annotation { "Feature Type Name" : "Feature", "Feature Type Description" : "" }
export const myFeature = defineFeature(function(context is Context, id is Id, definition is map)
    precondition{}
    {
        {
            var Q0;
            Q0=qCreatedBy(makeId("Front.planeOp"),FACE);
            var sketch = newSketch(context, id + "F0", { "sketchPlane" : qUnion([Q0])});
            skLineSegment(sketch, "E0.bottom", {"start": v(-78.74, 0) * mm, "end": v(0, 0) * mm});
            skLineSegment(sketch, "E0.top", {"start": v(-56.51, 177.8) * mm, "end": v(0, 177.8) * mm});
            skLineSegment(sketch, "E0.left", {"start": v(0, 177.8) * mm, "end": v(0, 0) * mm});
            skLineSegment(sketch, "E0.right", {"start": v(-78.74, 155.58) * mm, "end": v(-78.74, 0) * mm});
            skArc(sketch, "E1", {"start": v(-56.51, 177.8) * mm, "mid": v(-72.23, 171.3) * mm, "end": v(-78.74, 155.58) * mm});
            skCircle(sketch, "E2", {"center": v(-46.99, 50.8) * mm, "radius": 22.23 * mm});
            skPoint(sketch, "E3", {"position": v(-61.34, 15.24) * mm});
            skPoint(sketch, "E4", {"position": v(-51.82, 15.24) * mm});
            skPoint(sketch, "E5", {"position": v(-61.34, 86.36) * mm});
            skPoint(sketch, "E6", {"position": v(-51.82, 86.36) * mm});
            skText(sketch, "E7", { "text": "FUEL TANK", "fontName": "Arimo-Regular.ttf"});
            skText(sketch, "E8", { "text": "OFF", "fontName": "Arimo-Regular.ttf"});
            skText(sketch, "E9", { "text": "L", "fontName": "Arimo-Regular.ttf"});
            skText(sketch, "E10", { "text": "R", "fontName": "Arimo-Regular.ttf"});
            skLineSegment(sketch, "E11.bottom", {"start": v(-78.74, -11.25) * mm, "end": v(0, -11.25) * mm});
            skLineSegment(sketch, "E11.top", {"start": v(-78.74, -55.7) * mm, "end": v(0, -55.7) * mm});
            skLineSegment(sketch, "E11.left", {"start": v(-78.74, -11.25) * mm, "end": v(-78.74, -55.7) * mm});
            skLineSegment(sketch, "E11.right", {"start": v(0, -11.25) * mm, "end": v(0, -55.7) * mm});
            skArc(sketch, "E12", {"start": v(-48.58, -22.48) * mm, "mid": v(-47, -44.6) * mm, "end": v(-45.4, -22.48) * mm});
            skLineSegment(sketch, "E13", {"start": v(-48.58, -20.45) * mm, "end": v(-45.4, -20.45) * mm});
            skLineSegment(sketch, "E14", {"start": v(-45.4, -20.45) * mm, "end": v(-45.4, -22.48) * mm});
            skPoint(sketch, "E15.endSnap0", {"position": v(-46.99, -22.37) * mm});
            skLineSegment(sketch, "E16", {"start": v(-48.58, -20.45) * mm, "end": v(-48.58, -22.48) * mm});
            const initialGuessF0  = {"E7": [-0.0617, 0.02223, 1, 0, 0.00381], "E8": [-0.05236, 0.07557, 1, 0, 0.0038], "E9": [-0.07489, 0.0508, 1, 0, 0.0038], "E10": [-0.02222, 0.0508, 1, 0, 0.00381]};
            skSetInitialGuess(sketch, initialGuessF0);
            skSolve(sketch);
        }
        {
            var Q0;
            Q0=makeQuery(id+"F0.imprint","IMPRINT",FACE,{"disambiguationData":[TD([[makeQuery(id+"F0.imprint","IMPRINT",EDGE,{"derivedFrom":sQuery(id+"F0.wireOp",EDGE,"E0.bottom")}),1.0]])]});
            extrude(context, id + "F1", {"entities" : qUnion([Q0]), "depth" : 3.17 * mm});
        }
        {
            var Q0;
            Q0=sQuery(id+"F0.wireOp",VERTEX,"E6");
            var Q1;
            Q1=sQuery(id+"F0.wireOp",VERTEX,"E5");
            var Q2;
            Q2=sQuery(id+"F0.wireOp",VERTEX,"E3");
            var Q3;
            Q3=sQuery(id+"F0.wireOp",VERTEX,"E4");
            var Q4;
            Q4=makeQuery(id+"F1.opExtrude","SWEPT_BODY",BODY,{"disambiguationData":[OSD([sQuery(id+"F0.wireOp",EDGE,"E0.bottom"),sQuery(id+"F0.wireOp",EDGE,"E0.top"),sQuery(id+"F0.wireOp",EDGE,"E0.left"),sQuery(id+"F0.wireOp",EDGE,"E0.right"),sQuery(id+"F0.wireOp",EDGE,"E1"),sQuery(id+"F0.wireOp",EDGE,"E2")])]});
            hole(context, id + "F2", {"style" : HoleStyle.SIMPLE, "endStyle" : HoleEndStyle.THROUGH, "oppositeDirection" : true, "holeDiameter" : 2.41 * mm, "isTappedThrough" : true, "tappedDepth" : 12.7 * mm, "tapClearance" : 3, "locations" : qUnion([Q0, Q1, Q2, Q3]), "scope" : qUnion([Q4])});
        }
        {
            var Q0;
            Q0=makeQuery(id+"F0.imprint","IMPRINT",FACE,{"disambiguationData":[TD([[makeQuery(id+"F0.imprint","IMPRINT",EDGE,{"derivedFrom":sQuery(id+"F0.wireOp",EDGE,"E8.sketch_text.stroke-11")}),1.0]])]});
            var Q1;
            Q1=makeQuery(id+"F0.imprint","IMPRINT",FACE,{"disambiguationData":[TD([[makeQuery(id+"F0.imprint","IMPRINT",EDGE,{"derivedFrom":sQuery(id+"F0.wireOp",EDGE,"E10.sketch_text.stroke-12")}),1.0]])]});
            var Q2;
            Q2=makeQuery(id+"F0.imprint","IMPRINT",FACE,{"disambiguationData":[TD([[makeQuery(id+"F0.imprint","IMPRINT",EDGE,{"derivedFrom":sQuery(id+"F0.wireOp",EDGE,"E7.sketch_text.stroke-60")}),1.0]])]});
            extrude(context, id + "F3", {"entities" : qUnion([Q0, Q1, Q2]), "depth" : 25.4 * mm});
        }
        {
            var Q0;
            Q0=makeQuery(id+"F0.imprint","IMPRINT",FACE,{"disambiguationData":[TD([[makeQuery(id+"F0.imprint","IMPRINT",EDGE,{"derivedFrom":sQuery(id+"F0.wireOp",EDGE,"E11.bottom")}),-1.0]])]});
            extrude(context, id + "F4", {"entities" : qUnion([Q0]), "depth" : 3.17 * mm});
        }
    });